# Revit family: Faucet-Lavatory-American_Standard-Paradigm_Selectronic-703B.2XX_Series
name_source: partatom
category: Plumbing Fixtures
units: mm (PartAtom-declared; Revit-internal decimal feet)

## family parameters
Always vertical = No
Cut with Voids When Loaded = No
OmniClass Number = 23.45.55.17
OmniClass Title = Mixing Faucets
Part Type = Normal
Room Calculation Point = No
Round Connector Dimension = Use Diameter
Shared = Yes
Work Plane-Based = Yes

## types (6) — shared parameters
605XRCW Remote Control = No
605XTMV1070 Thermostatic Mixing Valve = No
703P400 - 4" Deck Plate = No
706P800 - 8" Deck Plate = No
ADA Compliant = Yes
Above-Deck Mixing = Yes
Assembly Code = D2020300
CW Connection = Yes
CWFU = 1.5
Compliance Certifications = These products meet or exceed the following codes and standards:ANSI A117.1, ASME A112.18.1/CSA B125.1,NSF/ANSI/CAN 372,NSF/ANSI/CAN 61
Default Elevation = 0"
Description = Paradigm™ Selectronic® Integrated Proximity Lavatory Faucet
Faucet Base Height = 0"
Faucet Reach Height = 6 5/8"
Faucet Reach Length = 5 1/2"
HW Connection = Yes
HWFU = 1.5
Height = 7 1/2"
Inlet Connection Diameter = 3/8"
Installation Type = Deck Mounted
Length = 7 1/2"
Manufacturer = American Standard
PK00.BBU Allows AC Powered Faucets to Continuously Operate During a Power Failure = No
PK00.HAC Hard-Wired AC Power Supply and 10" Extension Cable = No
PK00.MAC Multi-AC Adapter and 10" Extension Cable = No
PK00.PAC Plug-In AC Power Supply and Single AC Adapter = No
PK00.WRK PWRX Battery Pack and Holder = No
Pressure Range = Water pressure range from 20 - 120 psi.
Product Documentation Link = https://lixil.cdn.celum.cloud
SmarTherm Safety Shut-Off = No
Tempered Water Connection = Yes
URL = http://www.americanstandard-us.com
Vent Connection = No
WFU = 2
Waste Connection = No
Width = 2"

## per-type parameters (varying)
| type | Finish | Flow Rate | Flow-Rate | Material |
| 703B203.002 | Metal-American Standard-002-Polished Chrome | 0.35 gpm (1.32 L/min) | 0 GPM | Metal-American Standard-002-Polished Chrome |
| 703B205.002 | Metal-American Standard-002-Polished Chrome | 0.5 gpm (1.89 L/min) | 1 GPM | Metal-American Standard-002-Polished Chrome |
| 703B205.295 | Metal-American Standard-295-Brushed Nickel | 0.5 gpm (1.89 L/min) | 1 GPM | Metal-American Standard-295-Brushed Nickel |
| 703B203.295 | Metal-American Standard-295-Brushed Nickel | 0.35 gpm (1.32 L/min) | 0 GPM | Metal-American Standard-295-Brushed Nickel |
| 703B205.243 | Metal-American Standard-243-Matte Black | 0.5 gpm (1.89 L/min) | 1 GPM | Metal-American Standard-243-Matte Black |
| 703B205.GN0 | Metal-American Standard-GN0-Brushed Cool Sunrise | 0.5 gpm (1.89 L/min) | 1 GPM | Metal-American Standard-GN0-Brushed Cool Sunrise |

note: column(s) folded — value = type name in every type: Model

## geometry (parser evidence)
native form markers: Sweep x4
no freeform markers — native parametric forms only
